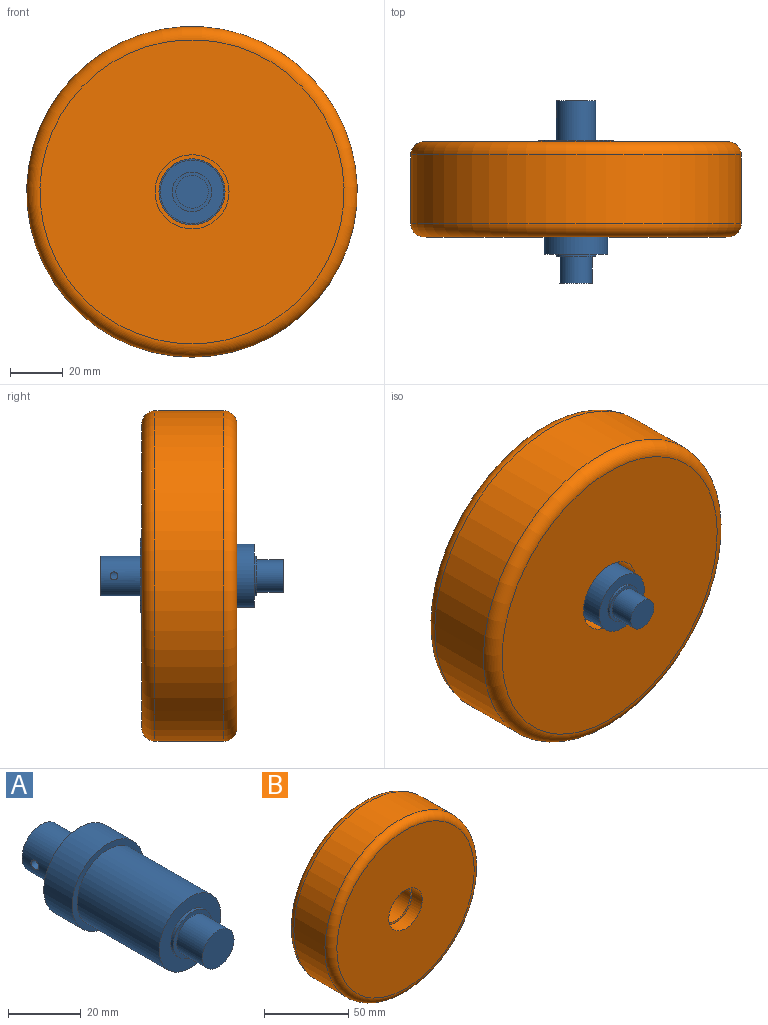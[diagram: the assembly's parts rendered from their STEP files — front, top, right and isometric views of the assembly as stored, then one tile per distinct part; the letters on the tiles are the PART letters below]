
ASSEMBLY  parts=2 mates=1
PART A: 14 faces, bbox 28x69x28 mm
  f0: cylinder r=14mm len=28mm, axis (0,1,0), area 967.6mm2, adj f1,f2
  f1: plane 28x28mm, normal (0,-1,0), area 163.4mm2, adj f0,f3
  f2: plane 28x28mm, normal (0,1,0), area 439mm2, adj f0,f6
  f3: cylinder r=12mm len=32mm, axis (0,1,0), area 2412.7mm2, adj f1,f4
  f4: plane 24x24mm, normal (0,-1,0), area 275.7mm2, adj f3,f9
  f5: cylinder r=4mm len=15mm, axis (0,-1,0), area 369.8mm2, adj f7,f8,f13
  f6: cylinder r=7.5mm len=15mm, axis (0,-1,0), area 699.7mm2, adj f2,f7,f13
  f7: plane 15x15mm, normal (0,1,0), area 126.4mm2, adj f5,f6
  f8: plane 8x8mm, normal (0,1,0), area 50.3mm2, adj f5
  f9: cylinder r=7.5mm len=15mm, axis (0,1,0), area 47.1mm2, adj f4,f10
  f10: plane 15x15mm, normal (0,-1,0), area 57.9mm2, adj f9,f11
  f11: cylinder r=6.15mm len=12.3mm, axis (0,1,0), area 386.4mm2, adj f10,f12
  f12: plane 12.3x12.3mm, normal (0,-1,0), area 118.8mm2, adj f11
  f13: cylinder r=1.5mm len=3.79mm, axis (1,0,0), area 33.6mm2, adj f5,f6
PART B: 10 faces, bbox 135.3x36x135.3 mm
  f0: cylinder r=12.5mm len=25mm, axis (0,1,0), area 1374.4mm2, adj f6,f8
  f1: cylinder r=62.5mm len=125mm, axis (0,1,0), area 10210.2mm2, adj f4,f5
  f2: plane 115x115mm, normal (0,-1,0), area 9771.1mm2, adj f5,f7
  f3: plane 115x115mm, normal (0,1,0), area 9771.1mm2, adj f4,f9
  f4: torus R=57.5mm, axis (0,-1,0), area 2994.6mm2, adj f1,f3
  f5: torus R=57.5mm, axis (0,-1,0), area 2994.6mm2, adj f1,f2
  f6: plane 28x28mm, normal (0,-1,0), area 124.9mm2, adj f0,f7
  f7: cylinder r=14mm len=28mm, axis (0,-1,0), area 747.7mm2, adj f2,f6
  f8: plane 28x28mm, normal (0,1,0), area 124.9mm2, adj f0,f9
  f9: cylinder r=14mm len=28mm, axis (0,1,0), area 879.6mm2, adj f3,f8
PLACE A t=(-40.03,-9.9,36.5)mm
PLACE B t=(-40.03,-10.4,36.5)mm
MATE revolute A.f0 <-> B.f0  axis (0,1,0) through (-40.03,-15.4,36.5)mm
